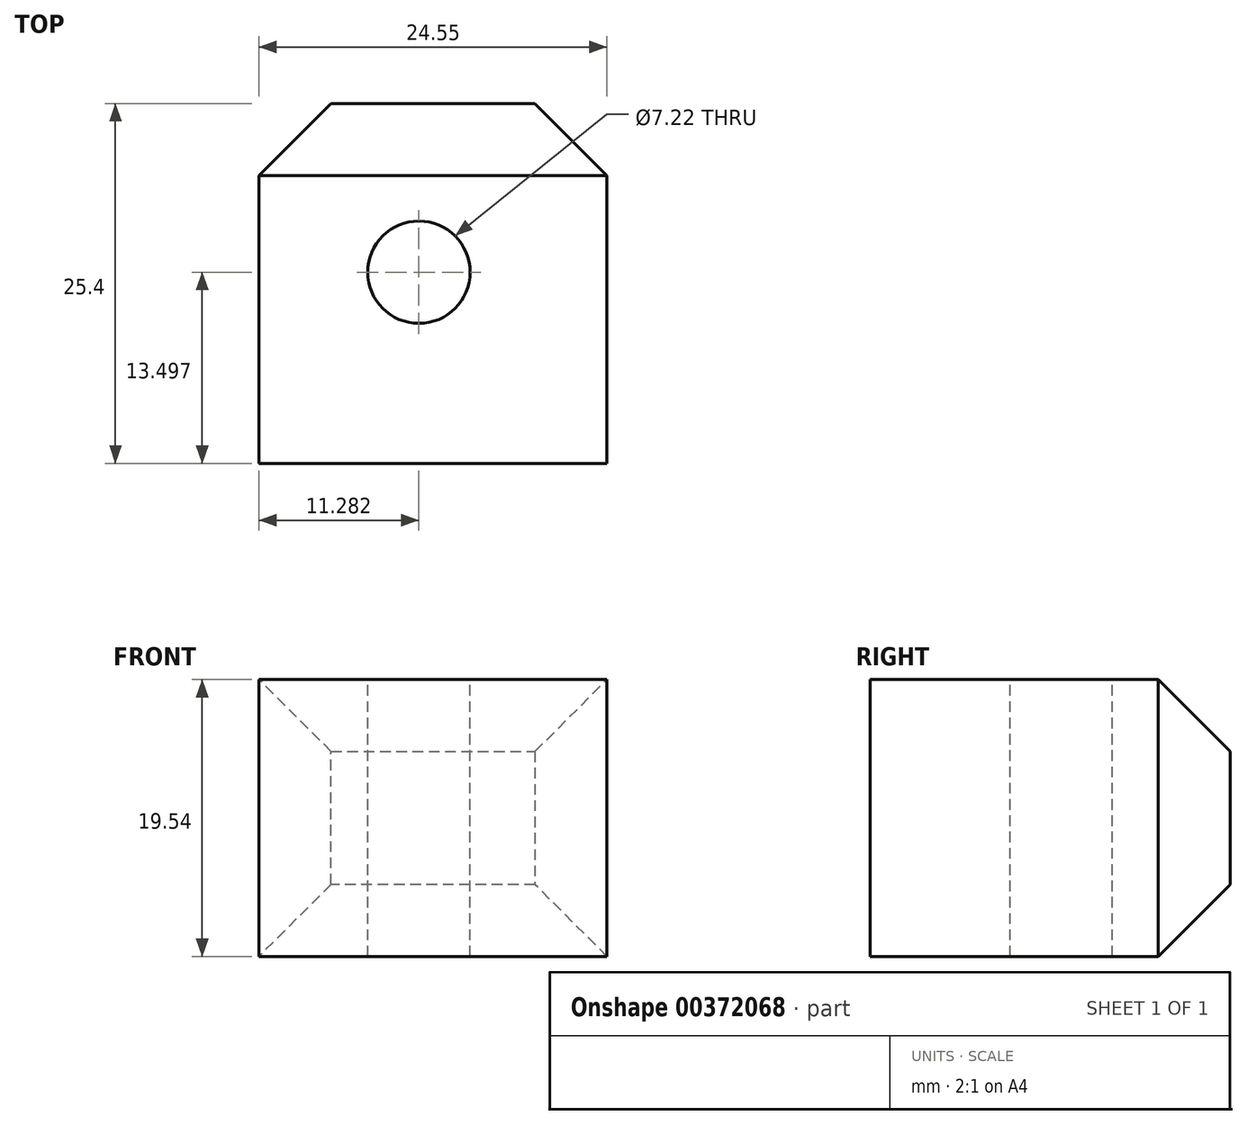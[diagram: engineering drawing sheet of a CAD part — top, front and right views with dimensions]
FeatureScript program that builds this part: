
annotation { "Feature Type Name" : "Feature", "Feature Type Description" : "" }
export const myFeature = defineFeature(function(context is Context, id is Id, definition is map)
    precondition{}
    {
        {
            var Q0;
            Q0=qCreatedBy(makeId("Front.planeOp"),FACE);
            var sketch = newSketch(context, id + "F0", { "sketchPlane" : qUnion([Q0])});
            skLineSegment(sketch, "E0.bottom", {"start": v(0, 0) * mm, "end": v(-24.55, 0) * mm});
            skLineSegment(sketch, "E0.top", {"start": v(0, 19.54) * mm, "end": v(-24.55, 19.54) * mm});
            skLineSegment(sketch, "E0.left", {"start": v(0, 0) * mm, "end": v(0, 19.54) * mm});
            skLineSegment(sketch, "E0.right", {"start": v(-24.55, 0) * mm, "end": v(-24.55, 19.54) * mm});
            skSolve(sketch);
        }
        {
            var Q0;
            Q0=makeQuery(id+"F0.imprint","IMPRINT",FACE,{"disambiguationData":[TD([[makeQuery(id+"F0.imprint","IMPRINT",EDGE,{"derivedFrom":sQuery(id+"F0.wireOp",EDGE,"E0.bottom")}),-1.0]])]});
            extrude(context, id + "F1", {"entities" : qUnion([Q0]), "depth" : 25.4 * mm});
        }
        {
            var Q0;
            Q0=makeQuery(id+"F1.opExtrude","CAP_FACE",FACE,{"disambiguationData":[OSD([sQuery(id+"F0.wireOp",EDGE,"E0.bottom"),sQuery(id+"F0.wireOp",EDGE,"E0.top"),sQuery(id+"F0.wireOp",EDGE,"E0.left"),sQuery(id+"F0.wireOp",EDGE,"E0.right")])],"isStart":true});
            chamfer(context, id + "F2", {"entities" : qUnion([Q0]), "width" : 5.08 * mm, "tangentPropagation" : true});
        }
        {
            var Q0;
            Q0=makeQuery(id+"F1.opExtrude","SWEPT_FACE",FACE,{"disambiguationData":[OSD([sQuery(id+"F0.wireOp",EDGE,"E0.top")])]});
            var sketch = newSketch(context, id + "F3", { "sketchPlane" : qUnion([Q0])});
            skCircle(sketch, "E1", {"center": v(-13.27, -11.9) * mm, "radius": 3.6 * mm});
            skSolve(sketch);
        }
        {
            var Q0;
            Q0=makeQuery(id+"F3.imprint","IMPRINT",FACE,{"disambiguationData":[TD([[makeQuery(id+"F3.imprint","IMPRINT",EDGE,{"derivedFrom":sQuery(id+"F3.wireOp",EDGE,"E1")}),1.0]])]});
            extrude(context, id + "F4", {"entities" : qUnion([Q0]), "operationType" : NewBodyOperationType.REMOVE, "endBound" : BoundingType.THROUGH_ALL, "oppositeDirection" : true, "depth" : 25.4 * mm});
        }
    });
